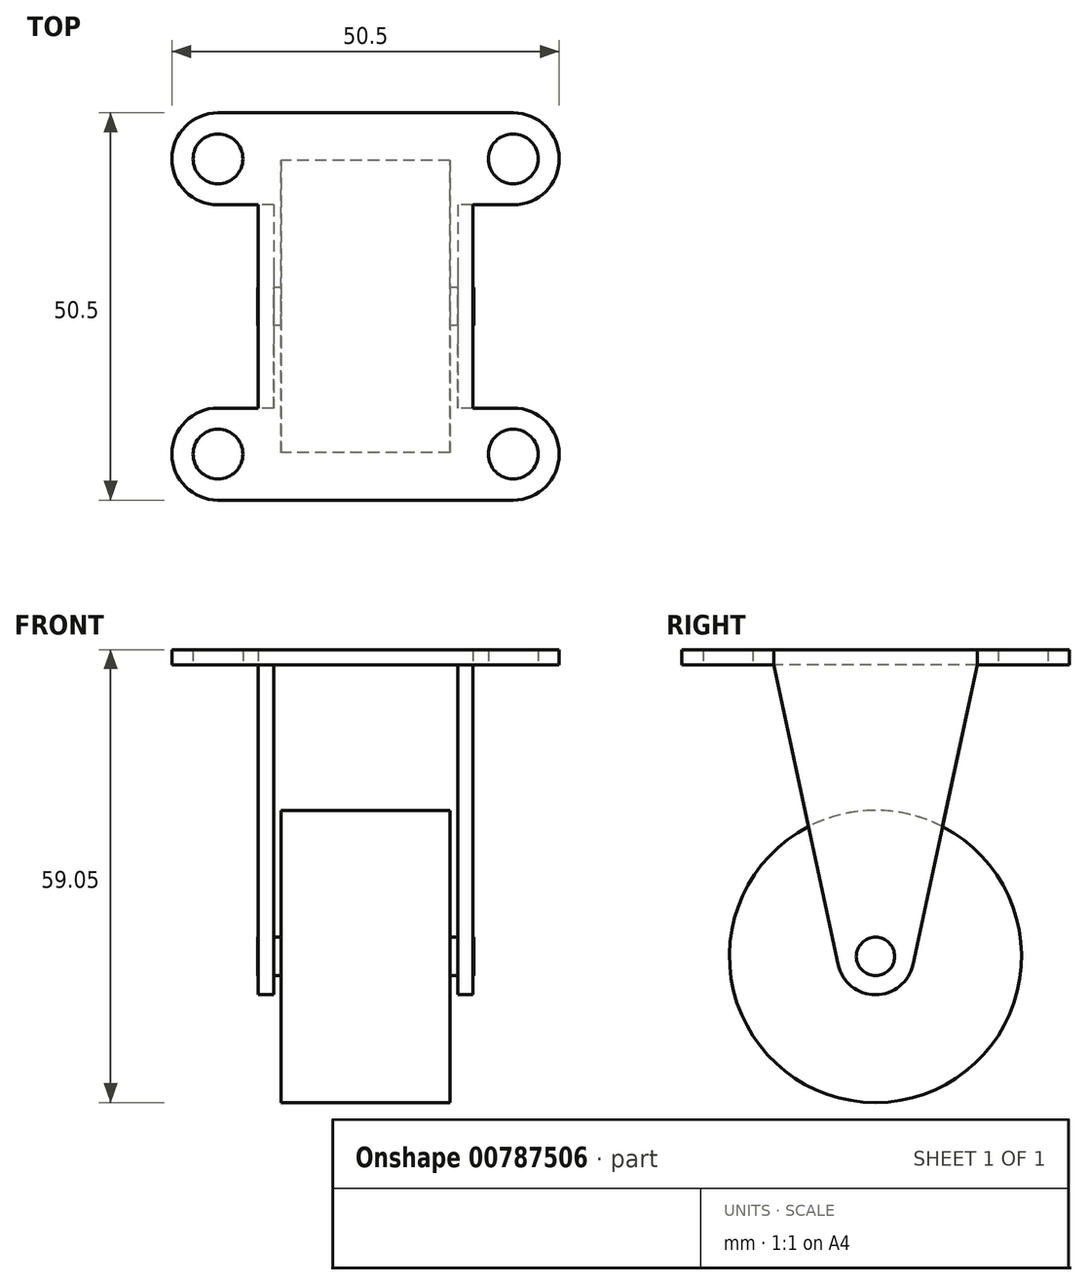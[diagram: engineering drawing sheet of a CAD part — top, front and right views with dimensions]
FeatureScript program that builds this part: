
annotation { "Feature Type Name" : "Feature", "Feature Type Description" : "" }
export const myFeature = defineFeature(function(context is Context, id is Id, definition is map)
    precondition{}
    {
        {
            var Q0;
            Q0=qCreatedBy(makeId("Top.planeOp"),FACE);
            var sketch = newSketch(context, id + "F0", { "sketchPlane" : qUnion([Q0])});
            skLineSegment(sketch, "E0.bottom", {"start": v(-31.62, 16.14) * mm, "end": v(6.88, 16.14) * mm});
            skLineSegment(sketch, "E0.top", {"start": v(-31.62, -34.36) * mm, "end": v(6.88, -34.36) * mm});
            skPoint(sketch, "E1.visualSharp", {"position": v(-37.62, 16.14) * mm});
            skArc(sketch, "E1.filletArc", {"start": v(-31.62, 16.14) * mm, "mid": v(-35.86, 14.38) * mm, "end": v(-37.62, 10.14) * mm});
            skPoint(sketch, "E2.visualSharp", {"position": v(12.88, 16.14) * mm});
            skArc(sketch, "E2.filletArc", {"start": v(12.88, 10.14) * mm, "mid": v(11.12, 14.38) * mm, "end": v(6.88, 16.14) * mm});
            skPoint(sketch, "E3.visualSharp", {"position": v(12.88, -34.36) * mm});
            skArc(sketch, "E3.filletArc", {"start": v(6.88, -34.36) * mm, "mid": v(11.12, -32.6) * mm, "end": v(12.88, -28.36) * mm});
            skPoint(sketch, "E4.visualSharp", {"position": v(-37.62, -34.36) * mm});
            skArc(sketch, "E4.filletArc", {"start": v(-37.62, -28.36) * mm, "mid": v(-35.86, -32.6) * mm, "end": v(-31.62, -34.36) * mm});
            skLineSegment(sketch, "E5", {"start": v(-31.62, 4.14) * mm, "end": v(-31.62, 4.14) * mm});
            skArc(sketch, "E6.filletArc", {"start": v(-37.62, 10.14) * mm, "mid": v(-35.86, 5.9) * mm, "end": v(-31.62, 4.14) * mm});
            skArc(sketch, "E7", {"start": v(-37.62, -28.36) * mm, "mid": v(-35.86, -24.12) * mm, "end": v(-31.62, -22.36) * mm});
            skArc(sketch, "E8", {"start": v(12.88, -28.36) * mm, "mid": v(11.12, -24.12) * mm, "end": v(6.88, -22.36) * mm});
            skArc(sketch, "E9", {"start": v(12.88, 10.14) * mm, "mid": v(11.12, 5.9) * mm, "end": v(6.88, 4.14) * mm});
            skCircle(sketch, "E10", {"center": v(-31.62, 10.14) * mm, "radius": 3.25 * mm});
            skCircle(sketch, "E11", {"center": v(6.88, 10.14) * mm, "radius": 3.25 * mm});
            skCircle(sketch, "E12", {"center": v(6.88, -28.36) * mm, "radius": 3.25 * mm});
            skCircle(sketch, "E13", {"center": v(-31.62, -28.36) * mm, "radius": 3.25 * mm});
            skLineSegment(sketch, "E14", {"start": v(-31.62, 4.14) * mm, "end": v(-26.37, 4.14) * mm});
            skLineSegment(sketch, "E15", {"start": v(-26.37, 4.14) * mm, "end": v(-26.37, -22.36) * mm});
            skLineSegment(sketch, "E16", {"start": v(-26.37, -22.36) * mm, "end": v(-31.62, -22.36) * mm});
            skLineSegment(sketch, "E17", {"start": v(6.88, 4.14) * mm, "end": v(1.63, 4.14) * mm});
            skLineSegment(sketch, "E18", {"start": v(1.63, 4.14) * mm, "end": v(1.63, -22.36) * mm});
            skLineSegment(sketch, "E19", {"start": v(1.63, -22.36) * mm, "end": v(6.88, -22.36) * mm});
            skSolve(sketch);
        }
        {
            var Q0;
            Q0=makeQuery(id+"F0.imprint","IMPRINT",FACE,{"disambiguationData":[TD([[makeQuery(id+"F0.imprint","IMPRINT",EDGE,{"derivedFrom":sQuery(id+"F0.wireOp",EDGE,"E0.bottom")}),-1.0]])]});
            extrude(context, id + "F1", {"entities" : qUnion([Q0]), "depth" : 2 * mm, "offsetDistance" : 25.4 * mm});
        }
        {
            var Q0;
            Q0=makeQuery(id+"F1.opExtrude","SWEPT_FACE",FACE,{"disambiguationData":[OSD([sQuery(id+"F0.wireOp",EDGE,"E15")])]});
            var sketch = newSketch(context, id + "F2", { "sketchPlane" : qUnion([Q0])});
            skLineSegment(sketch, "E20", {"start": v(-4.14, 2) * mm, "end": v(22.36, 2) * mm});
            skLineSegment(sketch, "E21", {"start": v(9.1, 2) * mm, "end": v(9.1, -38) * mm, "construction": true});
            skCircle(sketch, "E22", {"center": v(9.1, -38) * mm, "radius": 2.5 * mm});
            skArc(sketch, "E23", {"start": v(4.22, -39.05) * mm, "mid": v(9.1, -43) * mm, "end": v(14, -39.05) * mm});
            skLineSegment(sketch, "E24", {"start": v(-4.14, 2) * mm, "end": v(-4.14, 0) * mm});
            skLineSegment(sketch, "E25", {"start": v(-4.14, 0) * mm, "end": v(4.22, -39.05) * mm});
            skLineSegment(sketch, "E26", {"start": v(22.36, 2) * mm, "end": v(22.36, 0) * mm});
            skLineSegment(sketch, "E27", {"start": v(22.36, 0) * mm, "end": v(14, -39.05) * mm});
            skSolve(sketch);
        }
        {
            var Q0;
            Q0=makeQuery(id+"F2.imprint","IMPRINT",FACE,{"disambiguationData":[TD([[makeQuery(id+"F2.imprint","IMPRINT",EDGE,{"derivedFrom":sQuery(id+"F2.wireOp",EDGE,"E22")}),-1.0]])]});
            extrude(context, id + "F3", {"entities" : qUnion([Q0]), "operationType" : NewBodyOperationType.ADD, "oppositeDirection" : true, "depth" : 2 * mm, "offsetDistance" : 25.4 * mm});
        }
        {
            var Q0;
            Q0=makeQuery(id+"F2.imprint","IMPRINT",FACE,{"disambiguationData":[TD([[makeQuery(id+"F2.imprint","IMPRINT",EDGE,{"derivedFrom":sQuery(id+"F2.wireOp",EDGE,"E22")}),-1.0]])]});
            extrude(context, id + "F4", {"entities" : qUnion([Q0]), "operationType" : NewBodyOperationType.ADD, "oppositeDirection" : true, "depth" : 28 * mm, "offsetDistance" : 25.4 * mm, "hasSecondDirection" : true, "secondDirectionOppositeDirection" : true, "secondDirectionDepth" : 26 * mm});
        }
        {
            var Q0;
            Q0=makeQuery(id+"F3.opExtrude","CAP_FACE",FACE,{"disambiguationData":[OSD([sQuery(id+"F0.wireOp",EDGE,"E15"),sQuery(id+"F2.wireOp",EDGE,"E22"),sQuery(id+"F2.wireOp",EDGE,"E23"),sQuery(id+"F2.wireOp",EDGE,"E25"),sQuery(id+"F2.wireOp",EDGE,"E27")])],"isStart":false});
            var sketch = newSketch(context, id + "F5", { "sketchPlane" : qUnion([Q0])});
            skCircle(sketch, "E28", {"center": v(-9.1, -38) * mm, "radius": 2.5 * mm});
            skCircle(sketch, "E29", {"center": v(-9.1, -38) * mm, "radius": 19.05 * mm});
            skSolve(sketch);
        }
        {
            var Q0;
            Q0=makeQuery(id+"F5.imprint","IMPRINT",FACE,{"disambiguationData":[TD([[makeQuery(id+"F5.imprint","IMPRINT",EDGE,{"derivedFrom":sQuery(id+"F5.wireOp",EDGE,"E28")}),-1.0]])]});
            extrude(context, id + "F6", {"entities" : qUnion([Q0]), "operationType" : NewBodyOperationType.ADD, "oppositeDirection" : true, "depth" : 2.1 * mm, "offsetDistance" : 25.4 * mm});
        }
        {
            var Q0;
            Q0=makeQuery(id+"F5.imprint","IMPRINT",FACE,{"disambiguationData":[TD([[makeQuery(id+"F5.imprint","IMPRINT",EDGE,{"derivedFrom":sQuery(id+"F5.wireOp",EDGE,"E28")}),-1.0]])]});
            extrude(context, id + "F7", {"entities" : qUnion([Q0]), "operationType" : NewBodyOperationType.ADD, "depth" : 26.1 * mm, "offsetDistance" : 25.4 * mm});
        }
        {
            var Q0;
            {var subQ5=makeQuery(id+"F3.opExtrude","CAP_EDGE",EDGE,{"disambiguationData":[OSD([sQuery(id+"F2.wireOp",EDGE,"E23")])],"isStart":false});Q0=makeQuery(id+"F5.imprint","IMPRINT",FACE,{"disambiguationData":[TD([[makeQuery(id+"F5.imprint","IMPRINT",EDGE,{"derivedFrom":subQ5}),1.0]])]});}
            var Q1;
            Q1=makeQuery(id+"F5.imprint","IMPRINT",FACE,{"disambiguationData":[TD([[makeQuery(id+"F5.imprint","IMPRINT",EDGE,{"derivedFrom":sQuery(id+"F5.wireOp",EDGE,"E28")}),1.0]])]});
            extrude(context, id + "F8", {"entities" : qUnion([Q0, Q1]), "operationType" : NewBodyOperationType.ADD, "depth" : 23 * mm, "offsetDistance" : 25.4 * mm, "hasSecondDirection" : true, "secondDirectionOppositeDirection" : false, "secondDirectionDepth" : 1 * mm});
        }
    });
